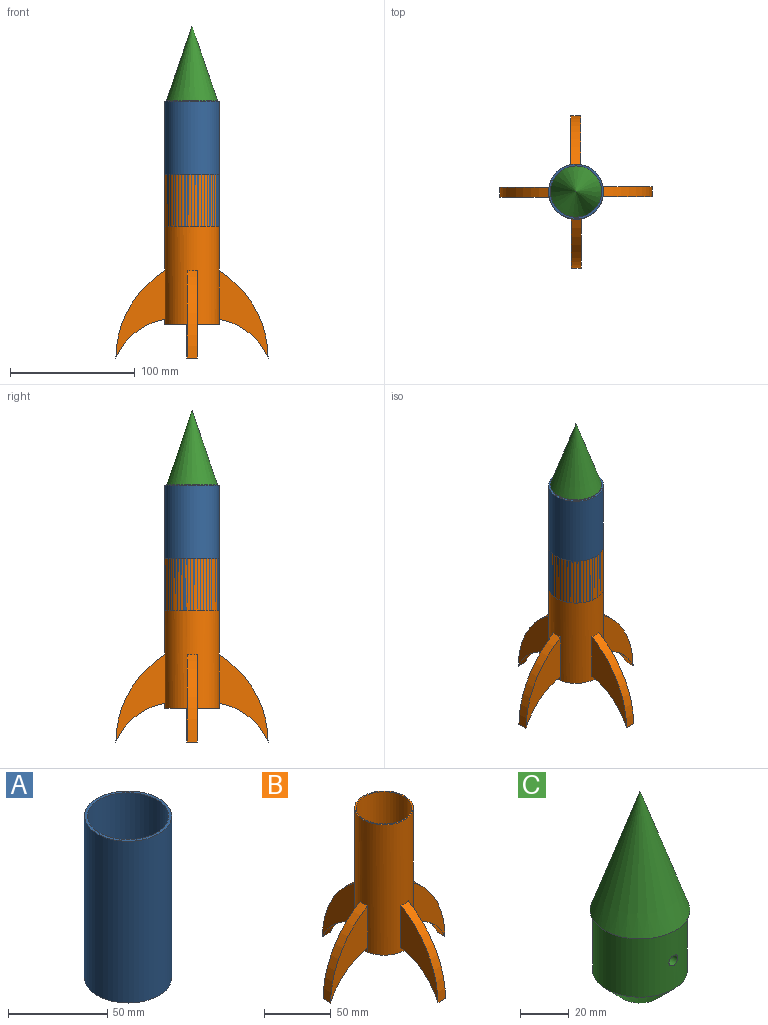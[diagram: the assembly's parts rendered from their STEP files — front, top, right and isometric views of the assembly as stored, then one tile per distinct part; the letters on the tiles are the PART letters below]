
ASSEMBLY  parts=3 mates=2
PART A: 4 faces, bbox 44x44x100 mm
  f0: cylinder r=22mm len=100mm, axis (0,0,-1), area 13823mm2, adj f1,f2
  f1: plane 44x44mm, normal (0,0,1), area 200.3mm2, adj f0,f3
  f2: plane 44x44mm, normal (0,0,-1), area 200.3mm2, adj f0,f3
  f3: cylinder r=20.5mm len=100mm, axis (0,0,1), area 12880.5mm2, adj f1,f2
PART B: 28 faces, bbox 122x122x146.9 mm
  f0: cylinder r=22mm len=120mm, axis (0,0,-1), area 15324.8mm2, adj f1,f2,f3,f4,f5,f7,f8,f9
  f1: cylinder r=51.98mm len=39.31mm, axis (0,-1,0), area 415.9mm2, adj f0,f2,f3,f7,f8
  f2: plane 4.04x0.59mm, normal (1,0,0), area 2.4mm2, adj f0,f1,f4,f8
  f3: cylinder r=81.98mm len=69.94mm, axis (0,-1,0), area 668.9mm2, adj f0,f1,f7,f8,f9
  f4: plane 44x44mm, normal (0,0,-1), area 135.2mm2, adj f0,f2,f6,f8,f12,f14,f19,f20
  f5: plane 44x44mm, normal (0,0,1), area 135.1mm2, adj f0,f6
  f6: cylinder r=21mm len=120mm, axis (0,0,1), area 15833.6mm2, adj f4,f5
  f7: plane 69.94x39.31mm, normal (0,-1,0), area 1119.1mm2, adj f0,f1,f3
  f8: plane 69.94x39.42mm, normal (0,1,0), area 1123.8mm2, adj f0,f1,f2,f3,f4,f9
  f9: plane 0.59x0.11mm, normal (0,0,1), area 0mm2, adj f0,f3,f8
  f10: plane 69.94x39.31mm, normal (1,0,0), area 1119.1mm2, adj f0,f13,f15
  f11: plane 0.59x0.11mm, normal (0,0,1), area 0mm2, adj f0,f12,f13
  f12: plane 69.94x39.42mm, normal (-1,0,0), area 1123.8mm2, adj f0,f4,f11,f13,f14,f15
  f13: cylinder r=81.98mm len=69.94mm, axis (1,0,0), area 668.9mm2, adj f0,f10,f11,f12,f15
  f14: plane 4.04x0.59mm, normal (0,1,0), area 2.4mm2, adj f0,f4,f12,f15
  f15: cylinder r=51.98mm len=39.31mm, axis (1,0,0), area 415.9mm2, adj f0,f10,f12,f13,f14
  f16: cylinder r=51.98mm len=39.31mm, axis (0,1,0), area 415.9mm2, adj f0,f17,f18,f19,f20
  f17: cylinder r=81.98mm len=69.94mm, axis (0,1,0), area 668.9mm2, adj f0,f16,f18,f20,f21
  f18: plane 69.94x39.31mm, normal (0,1,0), area 1119.1mm2, adj f0,f16,f17
  f19: plane 4.04x0.59mm, normal (-1,0,0), area 2.4mm2, adj f0,f4,f16,f20
  f20: plane 69.94x39.42mm, normal (0,-1,0), area 1123.8mm2, adj f0,f4,f16,f17,f19,f21
  f21: plane 0.59x0.11mm, normal (0,0,1), area 0mm2, adj f0,f17,f20
  f22: cylinder r=51.98mm len=39.31mm, axis (-1,0,0), area 415.9mm2, adj f0,f23,f24,f25,f26
  f23: plane 4.04x0.59mm, normal (0,-1,0), area 2.4mm2, adj f0,f4,f22,f26
  f24: cylinder r=81.98mm len=69.94mm, axis (-1,0,0), area 668.9mm2, adj f0,f22,f25,f26,f27
  f25: plane 69.94x39.31mm, normal (-1,0,0), area 1119.1mm2, adj f0,f22,f24
  f26: plane 69.94x39.42mm, normal (1,0,0), area 1123.8mm2, adj f0,f4,f22,f23,f24,f27
  f27: plane 0.59x0.11mm, normal (0,0,1), area 0mm2, adj f0,f24,f26
PART C: 6 faces, bbox 41x41x100 mm
  f0: plane 41x41mm, normal (0,0,-1), area 125.7mm2, adj f1,f2
  f1: cone r=0mm half-angle=18.9deg, axis (0,0,-1), area 4083.5mm2, adj f0
  f2: cylinder r=19.5mm len=39mm, axis (0,0,1), area 3636.5mm2, adj f0,f4,f5
  f3: plane 19x19mm, normal (0,0,-1), area 283.5mm2, adj f4
  f4: cone r=9.5mm half-angle=45deg, axis (0,0,1), area 1288.4mm2, adj f2,f3
  f5: cylinder r=2.5mm len=39mm, axis (0,-1,0), area 610.1mm2, adj f2
PLACE A t=(-35.11,-3.56,-45.22)mm
PLACE B t=(-35.11,-3.56,-124.09)mm
PLACE C t=(-35.11,-3.56,55.25)mm
MATE cylindrical B.f6 <-> A.f3  axis (0,0,1) through (-35.11,-3.56,-4.09)mm
MATE cylindrical C.f2 <-> A.f3  axis (0,0,-1) through (-35.11,-3.56,15.25)mm
